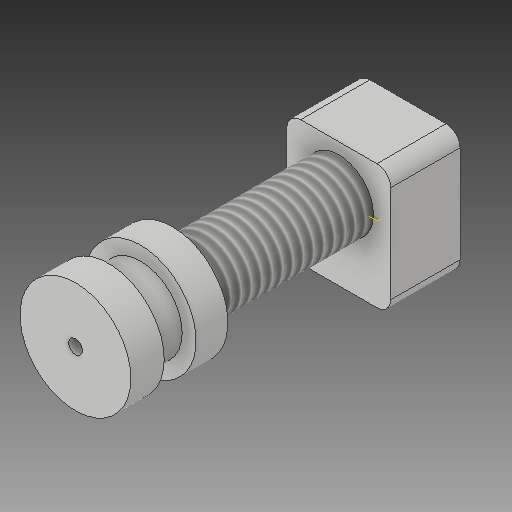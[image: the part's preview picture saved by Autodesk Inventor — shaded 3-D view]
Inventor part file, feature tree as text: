
AUTODESK INVENTOR PART (.ipt)
format: ipt  version: 2018 (Build 220112000, 112)  size: 189,440 bytes
history: native  units: mm
features: sketch x10, other x3, plane x1
ambient origin geometry x8: Origin, YZ Plane, XZ Plane, XY Plane, X Axis, Y Axis, Z Axis, Center Point
bodies: Solid1 (feature_tree)
feature tree (14):
  other  "Hotend Mock Up_MIR.ipt"
  other  "Solid1::Hotend Mock Up_MIR.ipt"
  other  "TaggingFeature1"
  sketch  "Sketch1"  dims[d0=10.0mm]
  sketch  "Sketch2"
  sketch  "Sketch3"
  sketch  "Sketch4"
  sketch  "Sketch5"
  sketch  "Sketch6"
  sketch  "Sketch7"
  sketch  "Sketch8"
  sketch  "Sketch9"
  sketch  "Sketch10"
  plane  "Work Plane1"
